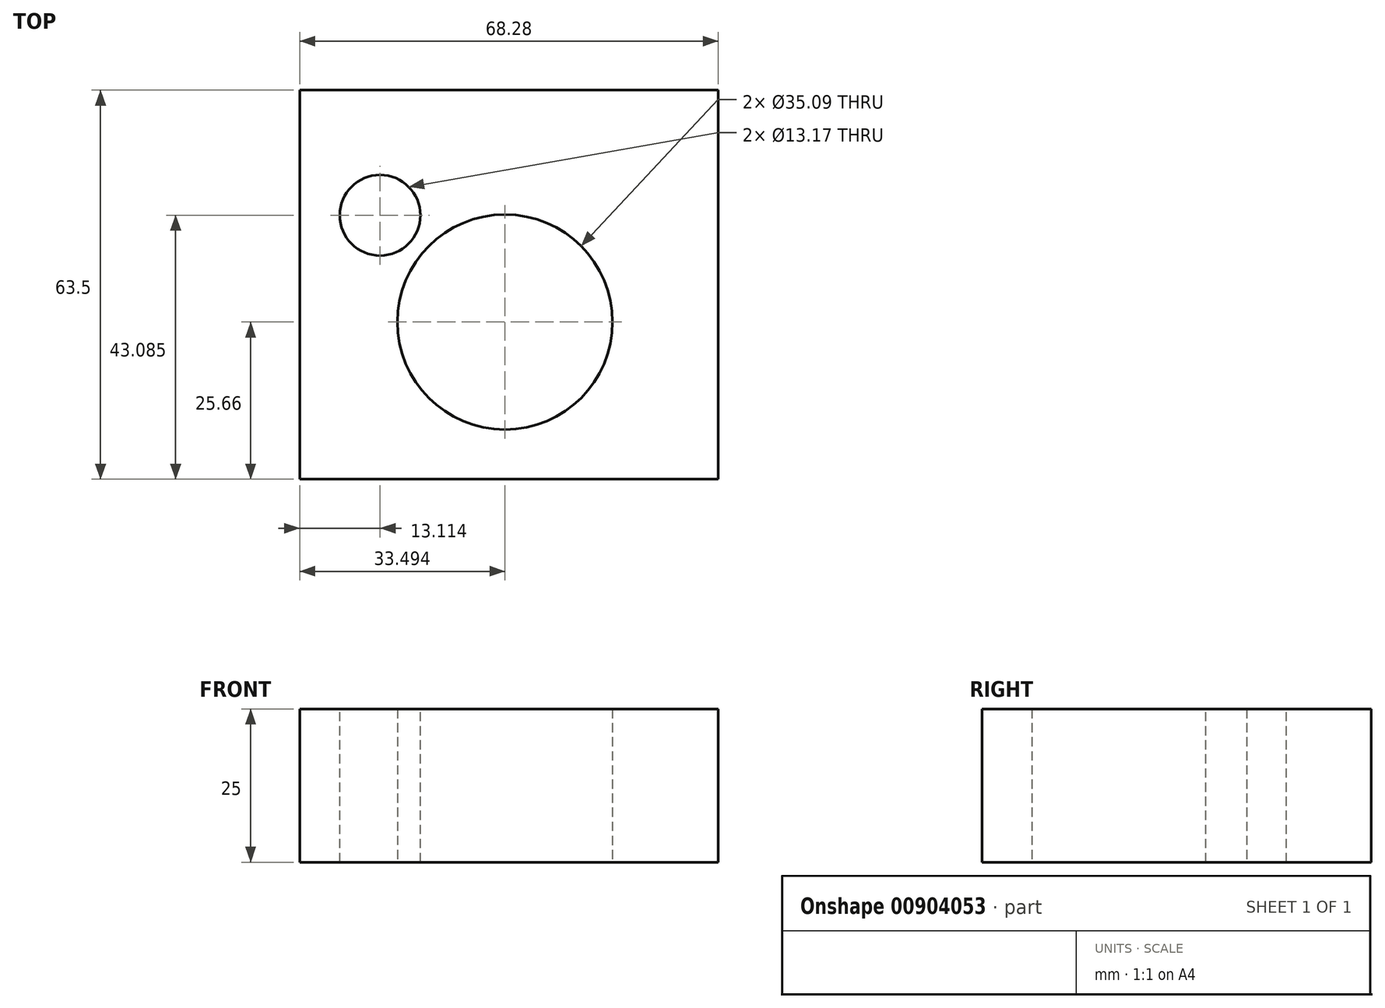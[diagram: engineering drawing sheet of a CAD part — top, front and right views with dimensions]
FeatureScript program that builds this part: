
annotation { "Feature Type Name" : "Feature", "Feature Type Description" : "" }
export const myFeature = defineFeature(function(context is Context, id is Id, definition is map)
    precondition{}
    {
        {
            var Q0;
            Q0=qCreatedBy(makeId("Top.planeOp"),FACE);
            var sketch = newSketch(context, id + "F0", { "sketchPlane" : qUnion([Q0])});
            skLineSegment(sketch, "E0.bottom", {"start": v(-41.97, 37.84) * mm, "end": v(26.31, 37.84) * mm});
            skLineSegment(sketch, "E0.top", {"start": v(-41.97, -25.66) * mm, "end": v(26.31, -25.66) * mm});
            skLineSegment(sketch, "E0.left", {"start": v(-41.97, 37.84) * mm, "end": v(-41.97, -25.66) * mm});
            skLineSegment(sketch, "E0.right", {"start": v(26.31, 37.84) * mm, "end": v(26.31, -25.66) * mm});
            skCircle(sketch, "E1", {"center": v(-8.48, 0) * mm, "radius": 17.55 * mm});
            skSolve(sketch);
        }
        {
            var Q0;
            Q0=makeQuery(id+"F0.imprint","IMPRINT",FACE,{"disambiguationData":[TD([[makeQuery(id+"F0.imprint","IMPRINT",EDGE,{"derivedFrom":sQuery(id+"F0.wireOp",EDGE,"E0.bottom")}),-1.0]])]});
            extrude(context, id + "F1", {"entities" : qUnion([Q0]), "depth" : 25 * mm, "offsetDistance" : 25 * mm});
        }
        {
            var Q0;
            Q0=makeQuery(id+"F1.opExtrude","CAP_FACE",FACE,{"disambiguationData":[OSD([sQuery(id+"F0.wireOp",EDGE,"E0.bottom"),sQuery(id+"F0.wireOp",EDGE,"E0.top"),sQuery(id+"F0.wireOp",EDGE,"E0.left"),sQuery(id+"F0.wireOp",EDGE,"E0.right"),sQuery(id+"F0.wireOp",EDGE,"E1")])],"isStart":false});
            var sketch = newSketch(context, id + "F2", { "sketchPlane" : qUnion([Q0])});
            skCircle(sketch, "E2", {"center": v(-28.86, 17.43) * mm, "radius": 6.58 * mm});
            skSolve(sketch);
        }
        {
            var Q0;
            Q0=makeQuery(id+"F2.imprint","IMPRINT",FACE,{"disambiguationData":[TD([[makeQuery(id+"F2.imprint","IMPRINT",EDGE,{"derivedFrom":sQuery(id+"F2.wireOp",EDGE,"E2")}),1.0]])]});
            extrude(context, id + "F3", {"entities" : qUnion([Q0]), "operationType" : NewBodyOperationType.REMOVE, "oppositeDirection" : true, "depth" : 25 * mm, "offsetDistance" : 25 * mm});
        }
    });
